# Revit family: Drain_Slot_2.25_Inch_Wide_Reveal-Zurn-Z891
name_source: partatom
category: Plumbing Fixtures
units: mm (PartAtom-declared; Revit-internal decimal feet)

## family parameters
Always vertical = Yes
Cut with Voids When Loaded = No
Maintain Annotation Orientation = No
OmniClass Number = 23.70.50.21.24.14
OmniClass Title = Deck Waste Water Drains
Part Type = Normal
Room Calculation Point = No
Round Connector Dimension = Use Radius
Shared = No
Work Plane-Based = No

## types (40) — shared parameters
Approx. Weight (Lbs) = 2
Assembly Code = D2030300
CW Connection = No
CWFU = 1
Connector Radius = 1 "
Default Elevation = 4 "
Description = 2-1/4 [57] WIDE REVEAL BY 60 [1524] LONG STAINLESS STEEL SLOTTED CHANNEL
HW Connection = No
HWFU = 1
Main Material = Steel - Zurn - Stainless - Type 304
Manufacturer = Zurn
Manufacturer Brand = Zurn Water, LLC
Modified Date = 08/26/2025
Outet offset = 3 "
Outlet Outer Diameter = 2.375 "
Outlet Outer Radius = 1.188 "
Outlet Size = 2 "
Product Documentation Link = https://files.zurn.com
Product Page URL = https://www.zurn.com
Product data url = https://www.bimobject.com
Thickness = 0.105 "
URL = http://www.zurn.com
Vent Connection = No
Waste Connection = Yes
zero-valued in all types: WFU

## per-type parameters (varying)
| type | Bottom Outlet | Deep Invert | End outlet | Flow | Shallow Invert | Type Comments |
| Z891-Z89101 | No | 4.63 " | No | 51 GPM | 4 " | Z891-89101-60 x 2.25 x 4.63 with V Bottom |
| Z891-Z89101 W/-E2 | No | 4.63 " | Yes | 0 GPM | 4 " | Z891-89101-60 x 2.25 x 4.63 with V Bottom with 2 Inch No-Hub End outlet |
| Z891-Z89101 W/-U2 | Yes | 4.63 " | No | 0 GPM | 4 " | Z891-89101-60 x 2.25 x 4.63 with V Bottom with 2 Inch No-Hub Bottom outlet |
| Z891-Z89101N | No | 4.63 " | No | 0 GPM | 4.63 " | Z891-89101N-60 x 2.25 x 5.25 with V Bottom |
| Z891-Z89102 | No | 5.25 " | No | 67 GPM | 4.63 " | Z891-89102-60 x 2.25 x 5.25 with V Bottom |
| Z891-Z89102 W/-E2 | No | 5.25 " | Yes | 0 GPM | 4.63 " | Z891-89102-60 x 2.25 x 5.25 with V Bottom with 2 Inch No-Hub End outlet |
| Z891-Z89102 W/-U2 | Yes | 5.25 " | No | 0 GPM | 4.63 " | Z891-89102-60 x 2.25 x 5.25 with V Bottom with 2 Inch No-Hub Bottom outlet |
| Z891-Z89102N | No | 5.25 " | No | 0 GPM | 5.25 " | Z891-89102N-60 x 2.25 x 5.25 with V Bottom |
| Z891-Z89103 | No | 5.88 " | No | 84 GPM | 5.25 " | Z891-89103-60 x 2.25 x 5.88 with V Bottom |
| Z891-Z89103 W/-E2 | No | 5.88 " | Yes | 0 GPM | 5.25 " | Z891-89103-60 x 2.25 x 5.88 with V Bottom with 2 Inch No-Hub End outlet |
| Z891-Z89103 W/-U2 | Yes | 5.88 " | No | 0 GPM | 5.25 " | Z891-89103-60 x 2.25 x 5.88 with V Bottom with 2 Inch No-Hub Bottom outlet |
| Z891-Z89103N | No | 5.88 " | No | 0 GPM | 5.88 " | Z891-89103N-60 x 2.25 x 5.88 with V Bottom |
| Z891-Z89104 | No | 6.5 " | No | 100 GPM | 5.88 " | Z891-89104-60 x 2.25 x 6.50 with V Bottom |
| Z891-Z89104 W/-E2 | No | 6.5 " | Yes | 0 GPM | 5.88 " | Z891-89104-60 x 2.25 x 6.50 with V Bottom with 2 Inch No-Hub End outlet |
| Z891-Z89104 W/-U2 | Yes | 6.5 " | No | 0 GPM | 5.88 " | Z891-89104-60 x 2.25 x 6.50 with V Bottom with 2 Inch No-Hub Bottom outlet |
| Z891-Z89104N | No | 6.5 " | No | 0 GPM | 6.5 " | Z891-89104N-60 x 2.25 x 6.50 with V Bottom |
| Z891-Z89105 | No | 7.13 " | No | 117 GPM | 6.5 " | Z891-89105-60 x 2.25 x 7.13 with V Bottom |
| Z891-Z89105 W/-E2 | No | 7.13 " | Yes | 0 GPM | 6.5 " | Z891-89105-60 x 2.25 x 7.13 with V Bottom with 2 Inch No-Hub End outlet |
| Z891-Z89105 W/-U2 | Yes | 7.13 " | No | 0 GPM | 6.5 " | Z891-89105-60 x 2.25 x 7.13 with V Bottom with 2 Inch No-Hub Bottom outlet |
| Z891-Z89105N | No | 7.13 " | No | 0 GPM | 7.13 " | Z891-89105N-60 x 2.25 x 7.13 with V Bottom |
| Z891-Z89106 | No | 7.75 " | No | 135 GPM | 7.13 " | Z891-89106-60 x 2.25 x 7.75 with V Bottom |
| Z891-Z89106 W/-E2 | No | 7.75 " | Yes | 0 GPM | 7.13 " | Z891-89106-60 x 2.25 x 7.75 with V Bottom with 2 Inch No-Hub End outlet |
| Z891-Z89106 W/-U2 | Yes | 7.75 " | No | 0 GPM | 7.13 " | Z891-89106-60 x 2.25 x 7.75 with V Bottom with 2 Inch No-Hub Bottom outlet |
| Z891-Z89106N | No | 7.75 " | No | 0 GPM | 7.75 " | Z891-89106N-60 x 2.25 x 7.75 with V Bottom |
| Z891-Z89107 | No | 8.38 " | No | 150 GPM | 7.75 " | Z891-89107-60 x 2.25 x 8.38 with V Bottom |
| Z891-Z89107 W/-E2 | No | 8.38 " | Yes | 0 GPM | 7.75 " | Z891-89107-60 x 2.25 x 8.38 with V Bottom with 2 Inch No-Hub End outlet |
| Z891-Z89107 W/-U2 | Yes | 8.38 " | No | 0 GPM | 7.75 " | Z891-89107-60 x 2.25 x 8.38 with V Bottom with 2 Inch No-Hub Bottom outlet |
| Z891-Z89107N | No | 8.38 " | No | 0 GPM | 8.38 " | Z891-89107N-60 x 2.25 x 8.38 with V Bottom |
| Z891-Z89108 | No | 9 " | No | 167 GPM | 8.38 " | Z891-89108-60 x 2.25 x 9.00 with V Bottom |
| Z891-Z89108 W/-E2 | No | 9 " | Yes | 0 GPM | 8.38 " | Z891-89108-60 x 2.25 x 9.00 with V Bottom with 2 Inch No-Hub End outlet |
| Z891-Z89108 W/-U2 | Yes | 9 " | No | 0 GPM | 8.38 " | Z891-89108-60 x 2.25 x 9.00 with V Bottom with 2 Inch No-Hub Bottom outlet |
| Z891-Z89108N | No | 9 " | No | 0 GPM | 9 " | Z891-89108N-60 x 2.25 x 9.00 with V Bottom |
| Z891-Z89109 | No | 9.63 " | No | 184 GPM | 9 " | Z891-89109-60 x 2.25 x 9.63 with V Bottom |
| Z891-Z89109 W/-E2 | No | 9.63 " | Yes | 0 GPM | 9 " | Z891-89109-60 x 2.25 x 9.63 with V Bottom with 2 Inch No-Hub End outlet |
| Z891-Z89109 W/-U2 | Yes | 9.63 " | No | 0 GPM | 9 " | Z891-89109-60 x 2.25 x 9.63 with V Bottom with 2 Inch No-Hub Bottom outlet |
| Z891-Z89109N | No | 9.63 " | No | 0 GPM | 9.63 " | Z891-89109N-60 x 2.25 x 9.63 with V Bottom |
| Z891-Z89110 | No | 10.25 " | No | 201 GPM | 9.63 " | Z891-89110-60 x 2.25 x 10.25 with V Bottom |
| Z891-Z89110 W/-E2 | No | 10.25 " | Yes | 0 GPM | 9.63 " | Z891-89110-60 x 2.25 x 10.25 with V Bottom with 2 Inch No-Hub End outlet |
| Z891-Z89110 W/-U2 | Yes | 10.25 " | No | 0 GPM | 9.63 " | Z891-89110-60 x 2.25 x 10.25 with V Bottom with 2 Inch No-Hub Bottom outlet |
| Z891-Z89110N | No | 10.25 " | No | 0 GPM | 10.25 " | Z891-89110N-60 x 2.25 x 10.25 with V Bottom |

note: column(s) folded — value = type name in every type: Model

## geometry (parser evidence)
native form markers: Blend x8, Sweep x7
no freeform markers — native parametric forms only
